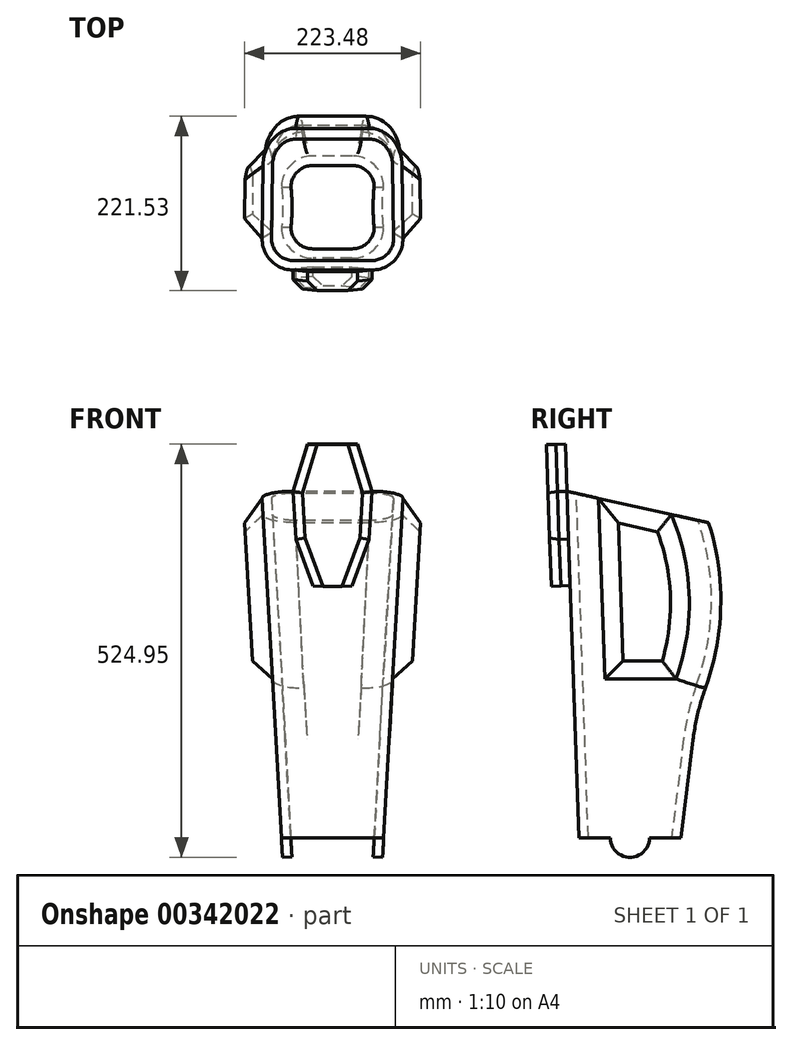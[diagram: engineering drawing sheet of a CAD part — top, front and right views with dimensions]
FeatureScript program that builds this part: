
annotation { "Feature Type Name" : "Feature", "Feature Type Description" : "" }
export const myFeature = defineFeature(function(context is Context, id is Id, definition is map)
    precondition{}
    {
        {
            var Q0;
            Q0=qCreatedBy(makeId("Right.planeOp"),FACE);
            var sketch = newSketch(context, id + "F0", { "sketchPlane" : qUnion([Q0])});
            skLineSegment(sketch, "E0", {"start": v(-65, -200) * mm, "end": v(65, -200) * mm});
            skLineSegment(sketch, "E1", {"start": v(-80, 200) * mm, "end": v(100, 200) * mm, "construction": true});
            skArc(sketch, "E2", {"start": v(96, -9.6) * mm, "mid": v(115.44, 94.87) * mm, "end": v(100, 200) * mm});
            skLineSegment(sketch, "E3", {"start": v(65, -200) * mm, "end": v(80.11, -75.9) * mm});
            skPoint(sketch, "E4.newPointA", {"position": v(89.35, 0) * mm});
            skArc(sketch, "E4.filletArc", {"start": v(96, -9.6) * mm, "mid": v(86.16, -42.3) * mm, "end": v(80.11, -75.9) * mm});
            skLineSegment(sketch, "E5", {"start": v(100, 200) * mm, "end": v(-80, 240) * mm});
            skLineSegment(sketch, "E6", {"start": v(-80, 240) * mm, "end": v(-65, -200) * mm});
            skSolve(sketch);
        }
        {
            var Q0;
            Q0=makeQuery(id+"F0.imprint","IMPRINT",FACE,{"disambiguationData":[TD([[makeQuery(id+"F0.imprint","IMPRINT",EDGE,{"derivedFrom":sQuery(id+"F0.wireOp",EDGE,"E0")}),1.0]])]});
            extrude(context, id + "F1", {"entities" : qUnion([Q0]), "depth" : 180 * mm});
        }
        {
            var Q0;
            Q0=qCreatedBy(makeId("Front.planeOp"),FACE);
            var sketch = newSketch(context, id + "F2", { "sketchPlane" : qUnion([Q0])});
            skLineSegment(sketch, "E7.0", {"start": v(180, -200) * mm, "end": v(155, -200) * mm});
            skLineSegment(sketch, "E8", {"start": v(90, -200) * mm, "end": v(90, 242.73) * mm, "construction": true});
            skLineSegment(sketch, "E9", {"start": v(155, -200) * mm, "end": v(180, 240) * mm});
            skLineSegment(sketch, "E10", {"start": v(25, -200) * mm, "end": v(0, 240) * mm});
            skLineSegment(sketch, "E11.0", {"start": v(180, 240) * mm, "end": v(180, -200) * mm});
            skLineSegment(sketch, "E12.0", {"start": v(0, 240) * mm, "end": v(0, -200) * mm});
            skLineSegment(sketch, "E13.trimOffspring", {"start": v(25, -200) * mm, "end": v(0, -200) * mm});
            skSolve(sketch);
        }
        {
            var Q0;
            Q0 = qSketchRegion(id + "F2", true);
            extrude(context, id + "F3", {"entities" : qUnion([Q0]), "operationType" : NewBodyOperationType.REMOVE, "endBound" : BoundingType.SYMMETRIC, "depth" : 250 * mm});
        }
        {
            var Q0;
            Q0=makeQuery(id+"F3.boolean.opBoolean","INTERSECT",EDGE,{"derivedFrom":[makeQuery(id+"F1.opExtrude","SWEPT_FACE",FACE,{"disambiguationData":[OSD([sQuery(id+"F0.wireOp",EDGE,"E6")])]}),makeQuery(id+"F3.opExtrude","SWEPT_FACE",FACE,{"disambiguationData":[OSD([sQuery(id+"F2.wireOp",EDGE,"E9")])]})]});
            var Q1;
            Q1=makeQuery(id+"F3.boolean.opBoolean","INTERSECT",EDGE,{"derivedFrom":[makeQuery(id+"F1.opExtrude","SWEPT_FACE",FACE,{"disambiguationData":[OSD([sQuery(id+"F0.wireOp",EDGE,"E2")])]}),makeQuery(id+"F3.opExtrude","SWEPT_FACE",FACE,{"disambiguationData":[OSD([sQuery(id+"F2.wireOp",EDGE,"E9")])]})]});
            var Q2;
            Q2=makeQuery(id+"F3.boolean.opBoolean","INTERSECT",EDGE,{"derivedFrom":[makeQuery(id+"F1.opExtrude","SWEPT_FACE",FACE,{"disambiguationData":[OSD([sQuery(id+"F0.wireOp",EDGE,"E2")])]}),makeQuery(id+"F3.opExtrude","SWEPT_FACE",FACE,{"disambiguationData":[OSD([sQuery(id+"F2.wireOp",EDGE,"E10")])]})]});
            var Q3;
            Q3=makeQuery(id+"F3.boolean.opBoolean","INTERSECT",EDGE,{"derivedFrom":[makeQuery(id+"F1.opExtrude","SWEPT_FACE",FACE,{"disambiguationData":[OSD([sQuery(id+"F0.wireOp",EDGE,"E6")])]}),makeQuery(id+"F3.opExtrude","SWEPT_FACE",FACE,{"disambiguationData":[OSD([sQuery(id+"F2.wireOp",EDGE,"E10")])]})]});
            fillet(context, id + "F4", {"entities" : qUnion([Q0, Q1, Q2, Q3]), "radius" : 40 * mm, "tangentPropagation" : true, "allowEdgeOverflow" : false});
        }
        {
            var Q0;
            Q0=makeQuery(id+"F1.opExtrude","SWEPT_FACE",FACE,{"disambiguationData":[OSD([sQuery(id+"F0.wireOp",EDGE,"E5")])]});
            var Q1;
            Q1=makeQuery(id+"F1.opExtrude","SWEPT_FACE",FACE,{"disambiguationData":[OSD([sQuery(id+"F0.wireOp",EDGE,"E0")])]});
            shell(context, id + "F5", {"entities" : qUnion([Q0, Q1]), "thickness" : 12 * mm});
        }
        {
            var Q0;
            Q0=makeQuery(id+"F3.boolean.opBoolean","COPY",FACE,{"derivedFrom":makeQuery(id+"F3.opExtrude","SWEPT_FACE",FACE,{"disambiguationData":[OSD([sQuery(id+"F2.wireOp",EDGE,"E9")])]})});
            var sketch = newSketch(context, id + "F6", { "sketchPlane" : qUnion([Q0])});
            skLineSegment(sketch, "E14.0", {"start": v(-39.75, 240.87) * mm, "end": v(-31.93, 11.26) * mm});
            skEllipticalArc(sketch, "E15.0", {});
            skLineSegment(sketch, "E16", {"start": v(58.4, 11.26) * mm, "end": v(-31.93, 11.26) * mm});
            skPoint(sketch, "E17.orphan", {"position": v(-25.05, -190.89) * mm});
            skLineSegment(sketch, "E18.0", {"start": v(-39.75, 240.87) * mm, "end": v(52.55, 220.32) * mm});
            const initialGuessF6  = {"E15.0": [-0.20813494311903946, 0.10838626882938608, 0, -1, 0.2840876672089078, 0.28363021358179186, 1.2218544432468381, 1.9757924383747814]};
            skSetInitialGuess(sketch, initialGuessF6);
            skSolve(sketch);
        }
        {
            var Q0;
            Q0=makeQuery(id+"F6.imprint","IMPRINT",FACE,{"disambiguationData":[TD([[makeQuery(id+"F6.imprint","IMPRINT",EDGE,{"derivedFrom":sQuery(id+"F6.wireOp",EDGE,"E14.0")}),1.0]])]});
            extrude(context, id + "F7", {"entities" : qUnion([Q0]), "operationType" : NewBodyOperationType.ADD, "depth" : 24 * mm});
        }
        {
            var Q0;
            Q0=makeQuery(id+"F7.opExtrude","CAP_EDGE",EDGE,{"disambiguationData":[OSD([sQuery(id+"F6.wireOp",EDGE,"E14.0")])],"isStart":false});
            var Q1;
            Q1=makeQuery(id+"F7.opExtrude","CAP_EDGE",EDGE,{"disambiguationData":[OSD([sQuery(id+"F6.wireOp",EDGE,"E18.0")])],"isStart":false});
            var Q2;
            Q2=makeQuery(id+"F7.opExtrude","CAP_EDGE",EDGE,{"disambiguationData":[OSD([sQuery(id+"F6.wireOp",EDGE,"E15.0")])],"isStart":false});
            var Q3;
            Q3=makeQuery(id+"F7.opExtrude","CAP_EDGE",EDGE,{"disambiguationData":[OSD([sQuery(id+"F6.wireOp",EDGE,"E16")])],"isStart":false});
            chamfer(context, id + "F8", {"entities" : qUnion([Q0, Q1, Q2, Q3]), "width" : 24 * mm, "tangentPropagation" : true});
        }
        {
            var Q0;
            Q0=makeQuery(id+"F3.boolean.opBoolean","COPY",FACE,{"derivedFrom":makeQuery(id+"F3.opExtrude","SWEPT_FACE",FACE,{"disambiguationData":[OSD([sQuery(id+"F2.wireOp",EDGE,"E10")])]})});
            var sketch = newSketch(context, id + "F9", { "sketchPlane" : qUnion([Q0])});
            skEllipticalArc(sketch, "E19.1", {});
            skLineSegment(sketch, "E20.0", {"start": v(31.93, 1.04) * mm, "end": v(39.75, 230.65) * mm});
            skLineSegment(sketch, "E21.0", {"start": v(39.75, 230.65) * mm, "end": v(-52.55, 210.11) * mm});
            skLineSegment(sketch, "E22", {"start": v(-58.4, 1.04) * mm, "end": v(31.93, 1.04) * mm});
            skPoint(sketch, "E23.orphan", {"position": v(25.05, -201.1) * mm});
            const initialGuessF9  = {"E19.1": [0.20813494311903946, 0.09817546462061881, 0, 1, 0.2840876672089078, 0.28363021358179186, 1.165800215215012, 1.919738210342955]};
            skSetInitialGuess(sketch, initialGuessF9);
            skSolve(sketch);
        }
        {
            var Q0;
            Q0=makeQuery(id+"F9.imprint","IMPRINT",FACE,{"disambiguationData":[TD([[makeQuery(id+"F9.imprint","IMPRINT",EDGE,{"derivedFrom":sQuery(id+"F9.wireOp",EDGE,"E19.1")}),1.0]])]});
            extrude(context, id + "F10", {"entities" : qUnion([Q0]), "operationType" : NewBodyOperationType.ADD, "depth" : 24 * mm});
        }
        {
            var Q0;
            Q0=makeQuery(id+"F10.opExtrude","CAP_EDGE",EDGE,{"disambiguationData":[OSD([sQuery(id+"F9.wireOp",EDGE,"E21.0")])],"isStart":false});
            var Q1;
            Q1=makeQuery(id+"F10.opExtrude","CAP_EDGE",EDGE,{"disambiguationData":[OSD([sQuery(id+"F9.wireOp",EDGE,"E20.0")])],"isStart":false});
            var Q2;
            Q2=makeQuery(id+"F10.opExtrude","CAP_EDGE",EDGE,{"disambiguationData":[OSD([sQuery(id+"F9.wireOp",EDGE,"E22")])],"isStart":false});
            var Q3;
            Q3=makeQuery(id+"F10.opExtrude","CAP_EDGE",EDGE,{"disambiguationData":[OSD([sQuery(id+"F9.wireOp",EDGE,"E19.1")])],"isStart":false});
            chamfer(context, id + "F11", {"entities" : qUnion([Q0, Q1, Q2, Q3]), "width" : 24 * mm, "tangentPropagation" : true});
        }
        {
            var Q0;
            Q0=makeQuery(id+"F1.opExtrude","SWEPT_FACE",FACE,{"disambiguationData":[OSD([sQuery(id+"F0.wireOp",EDGE,"E6")])]});
            var sketch = newSketch(context, id + "F12", { "sketchPlane" : qUnion([Q0])});
            skLineSegment(sketch, "E24.0", {"start": v(39.99, 242.59) * mm, "end": v(43.44, 181.83) * mm});
            skLineSegment(sketch, "E25", {"start": v(65, 122.59) * mm, "end": v(115, 122.59) * mm});
            skLineSegment(sketch, "E26", {"start": v(58.04, 302.59) * mm, "end": v(121.96, 302.59) * mm});
            skLineSegment(sketch, "E27", {"start": v(140.01, 242.59) * mm, "end": v(121.96, 302.59) * mm});
            skLineSegment(sketch, "E28", {"start": v(39.99, 242.59) * mm, "end": v(58.04, 302.59) * mm});
            skLineSegment(sketch, "E29", {"start": v(65, 122.59) * mm, "end": v(43.44, 181.83) * mm});
            skLineSegment(sketch, "E30", {"start": v(115, 122.59) * mm, "end": v(136.56, 181.83) * mm});
            skPoint(sketch, "E31.orphan", {"position": v(64.99, -197.67) * mm});
            skLineSegment(sketch, "E32.trimOffspring", {"start": v(136.56, 181.83) * mm, "end": v(140.01, 242.59) * mm});
            skPoint(sketch, "E33.0.start.orphan", {"position": v(115.01, -197.67) * mm});
            skSolve(sketch);
        }
        {
            var Q0;
            Q0=makeQuery(id+"F12.imprint","IMPRINT",FACE,{"disambiguationData":[TD([[makeQuery(id+"F12.imprint","IMPRINT",EDGE,{"derivedFrom":sQuery(id+"F12.wireOp",EDGE,"E24.0")}),1.0]])]});
            var Q1;
            Q1=makeQuery(id+"F12.imprint","IMPRINT",FACE,{"disambiguationData":[TD([[makeQuery(id+"F12.imprint","IMPRINT",EDGE,{"derivedFrom":sQuery(id+"F12.wireOp",EDGE,"E26")}),-1.0]])]});
            extrude(context, id + "F13", {"entities" : qUnion([Q0, Q1]), "operationType" : NewBodyOperationType.ADD, "depth" : 24 * mm});
        }
        {
            var Q0;
            Q0=makeQuery(id+"F13.opExtrude","CAP_EDGE",EDGE,{"disambiguationData":[OSD([sQuery(id+"F12.wireOp",EDGE,"E29")])],"isStart":false});
            var Q1;
            Q1=makeQuery(id+"F13.opExtrude","CAP_EDGE",EDGE,{"disambiguationData":[OSD([sQuery(id+"F12.wireOp",EDGE,"E30")])],"isStart":false});
            var Q2;
            Q2=makeQuery(id+"F13.opExtrude","CAP_EDGE",EDGE,{"disambiguationData":[OSD([sQuery(id+"F12.wireOp",EDGE,"E32.trimOffspring")])],"isStart":false});
            var Q3;
            Q3=makeQuery(id+"F13.opExtrude","CAP_EDGE",EDGE,{"disambiguationData":[OSD([sQuery(id+"F12.wireOp",EDGE,"E27")])],"isStart":false});
            var Q4;
            Q4=makeQuery(id+"F13.opExtrude","CAP_EDGE",EDGE,{"disambiguationData":[OSD([sQuery(id+"F12.wireOp",EDGE,"E28")])],"isStart":false});
            var Q5;
            Q5=makeQuery(id+"F13.opExtrude","CAP_EDGE",EDGE,{"disambiguationData":[OSD([sQuery(id+"F12.wireOp",EDGE,"E24.0")])],"isStart":false});
            chamfer(context, id + "F14", {"entities" : qUnion([Q0, Q1, Q2, Q3, Q4, Q5]), "width" : 12 * mm, "tangentPropagation" : true});
        }
        {
            var Q0;
            Q0=makeQuery(id+"F3.boolean.opBoolean","COPY",FACE,{"derivedFrom":makeQuery(id+"F3.opExtrude","SWEPT_FACE",FACE,{"disambiguationData":[OSD([sQuery(id+"F2.wireOp",EDGE,"E9")])]})});
            var sketch = newSketch(context, id + "F15", { "sketchPlane" : qUnion([Q0])});
            skArc(sketch, "E34", {"start": v(-25.05, -190.89) * mm, "mid": v(-0.04, -215.9) * mm, "end": v(24.98, -190.89) * mm});
            skLineSegment(sketch, "E35.0", {"start": v(-25.05, -190.89) * mm, "end": v(24.98, -190.89) * mm});
            skSolve(sketch);
        }
        {
            var Q0;
            Q0 = qSketchRegion(id + "F15", true);
            extrude(context, id + "F16", {"entities" : qUnion([Q0]), "operationType" : NewBodyOperationType.ADD, "oppositeDirection" : true, "depth" : 12 * mm});
        }
        {
            var Q0;
            Q0=makeQuery(id+"F3.boolean.opBoolean","COPY",FACE,{"derivedFrom":makeQuery(id+"F3.opExtrude","SWEPT_FACE",FACE,{"disambiguationData":[OSD([sQuery(id+"F2.wireOp",EDGE,"E10")])]})});
            var sketch = newSketch(context, id + "F17", { "sketchPlane" : qUnion([Q0])});
            skArc(sketch, "E36", {"start": v(-24.98, -201.1) * mm, "mid": v(0.04, -226.11) * mm, "end": v(25.05, -201.1) * mm});
            skLineSegment(sketch, "E37.0", {"start": v(25.05, -201.1) * mm, "end": v(-24.98, -201.1) * mm});
            skSolve(sketch);
        }
        {
            var Q0;
            Q0 = qSketchRegion(id + "F17", true);
            extrude(context, id + "F18", {"entities" : qUnion([Q0]), "operationType" : NewBodyOperationType.ADD, "oppositeDirection" : true, "depth" : 12 * mm});
        }
    });
